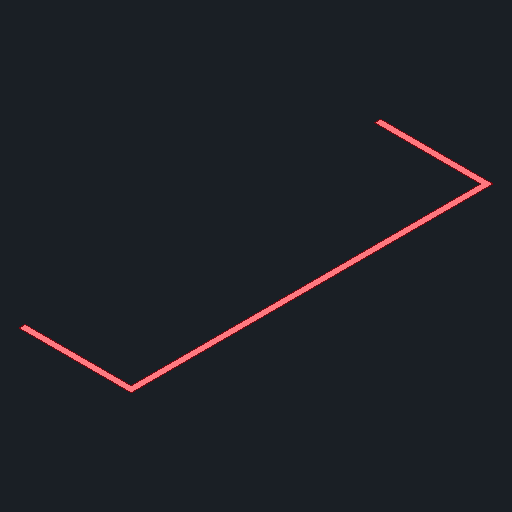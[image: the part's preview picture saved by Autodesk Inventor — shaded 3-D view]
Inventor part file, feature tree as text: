
AUTODESK INVENTOR PART (.ipt)
format: ipt  version: 2024 (Build 280153000, 153)  size: 84,480 bytes
history: native  units: in
note: dims shown in document units (in); Inventor stores cm internally (conversion verified against a paired STEP export)
features: extrude x1
ambient origin geometry x8: Origin, YZ Plane, XZ Plane, XY Plane, X Axis, Y Axis, Z Axis, Center Point
bodies: Solid1 (feature_tree)
feature tree (1):
  extrude  "Extrude-Thin1"  [1 undecoded]
note: 1 required parameter value undecoded (feature->parameter linkage not recoverable at this tier; creation-order binding heuristic only, values carry confidence <= 0.55)
